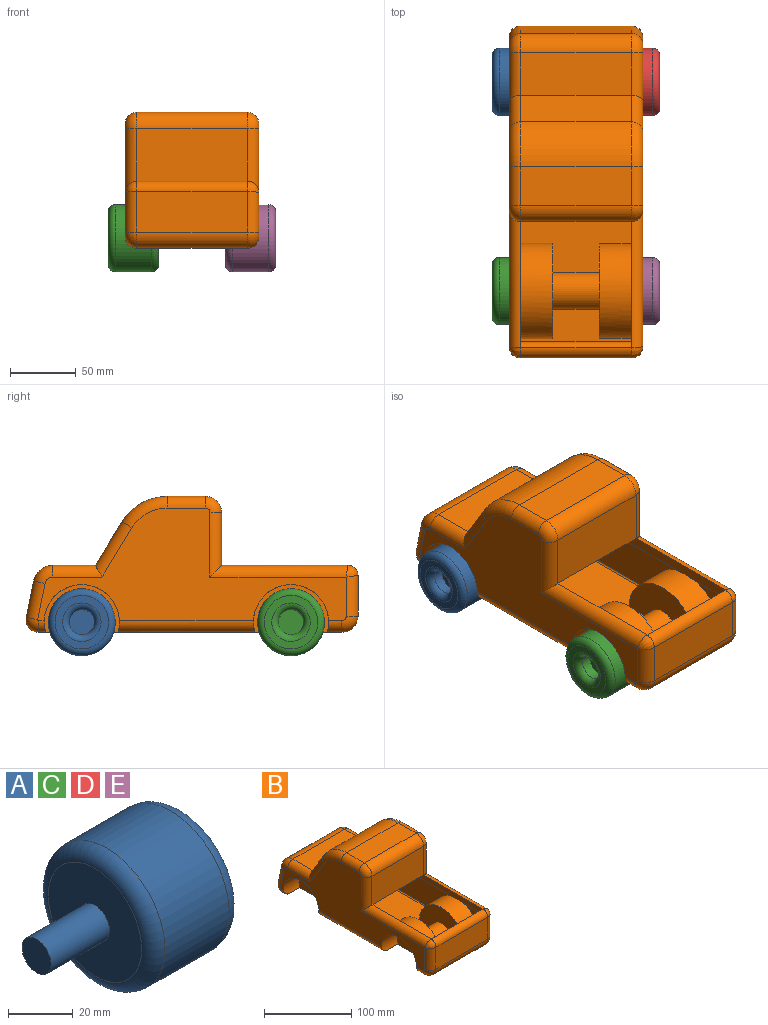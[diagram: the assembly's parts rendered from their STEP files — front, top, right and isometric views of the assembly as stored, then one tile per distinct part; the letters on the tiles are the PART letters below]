
ASSEMBLY  parts=5 mates=4
PART A: 10 faces, bbox 63.5x55x55 mm
  f0: cylinder r=6.35mm len=25.4mm, axis (-1,0,0), area 1013.4mm2, adj f1,f4
  f1: plane 12.7x12.7mm, normal (-1,0,0), area 126.7mm2, adj f0
  f2: cylinder r=25.4mm len=50.8mm, axis (-1,0,0), area 4459mm2, adj f8,f9
  f3: plane 40.64x40.64mm, normal (1,0,0), area 627.1mm2, adj f7,f9
  f4: plane 40.64x40.64mm, normal (-1,0,0), area 1170.5mm2, adj f0,f8
  f5: cylinder r=9.53mm len=19.05mm, axis (1,0,0), area 456mm2, adj f6,f7
  f6: plane 19.05x19.05mm, normal (1,0,0), area 285mm2, adj f5
  f7: torus R=14.61mm, axis (1,0,0), area 570.1mm2, adj f3,f5
  f8: torus R=20.32mm, axis (1,0,0), area 1180.9mm2, adj f2,f4
  f9: torus R=20.32mm, axis (1,0,0), area 1180.9mm2, adj f2,f3
PART B: 126 faces, bbox 101.6x251.9x106.5 mm
  f0: plane 234.13x85.37mm, normal (-1,0,0), area 8596.9mm2, adj f20,f22,f25,f26,f27,f29,f30,f31
  f1: cylinder r=40.13mm len=83.82mm, axis (-1,0,0), area 3441.9mm2, adj f2,f13,f33,f48
  f2: plane 83.82x29.03mm, normal (0,0,1), area 2433.6mm2, adj f1,f3,f32,f47
  f3: cylinder r=12.28mm len=83.82mm, axis (-1,0,0), area 1617.1mm2, adj f2,f4,f31,f46
  f4: plane 83.82x40.06mm, normal (0,-1,0), area 3358.1mm2, adj f3,f30,f45,f83
  f5: cylinder r=7.7mm len=83.82mm, axis (-1,0,0), area 1014.3mm2, adj f6,f28,f43,f76
  f6: plane 83.82x30.81mm, normal (0,-1,0), area 2582.8mm2, adj f5,f7,f27,f42
  f7: cylinder r=12.28mm len=83.82mm, axis (-1,0,0), area 1617.1mm2, adj f6,f8,f26,f41
  f8: plane 230.21x83.82mm, normal (0,0,-1), area 15669.6mm2, adj f7,f9,f15,f16,f17,f18,f19,f20
  f9: cylinder r=9.41mm len=83.82mm, axis (-1,0,0), area 1396.9mm2, adj f8,f10,f38,f53
  f10: plane 83.82x27.51mm, normal (0,0.98,0.2), area 2352.1mm2, adj f9,f11,f37,f52
  f11: cylinder r=14.98mm len=83.82mm, axis (-1,0,0), area 1722.4mm2, adj f10,f12,f36,f51
  f12: plane 83.82x32.24mm, normal (0,0,1), area 2702.5mm2, adj f11,f13,f35,f50
  f13: plane 83.82x33.11mm, normal (0,0.85,0.52), area 3250.5mm2, adj f1,f12,f34,f49
  f14: plane 234.13x85.37mm, normal (1,0,0), area 8624.5mm2, adj f16,f18,f40,f41,f42,f44,f45,f46
  f15: plane 57.15x36.2mm, normal (1,0,0), area 1586.2mm2, adj f8,f16,f23
  f16: cylinder r=28.57mm len=57.15mm, axis (1,0,0), area 2637.4mm2, adj f8,f14,f15,f54,f56
  f17: plane 56.52x35.88mm, normal (1,0,0), area 1552.9mm2, adj f8,f18,f24
  f18: cylinder r=28.26mm len=56.52mm, axis (1,0,0), area 2612.1mm2, adj f8,f14,f17,f40,f56
  f19: plane 57.15x36.2mm, normal (-1,0,0), area 1586.2mm2, adj f8,f20,f23
  f20: cylinder r=28.57mm len=57.15mm, axis (-1,0,0), area 2637.4mm2, adj f0,f8,f19,f39,f55
  f21: plane 57.15x36.2mm, normal (-1,0,0), area 1586.2mm2, adj f8,f22,f24
  f22: cylinder r=28.57mm len=57.15mm, axis (-1,0,0), area 2637.4mm2, adj f0,f8,f21,f25,f55
  f23: cylinder r=6.35mm len=50.8mm, axis (-1,0,0), area 2026.8mm2, adj f15,f19
  f24: cylinder r=6.35mm len=50.8mm, axis (-1,0,0), area 2026.8mm2, adj f17,f21
  f25: cylinder r=8.89mm len=10.98mm, axis (0,1,0), area 145.5mm2, adj f0,f8,f22,f26
  f26: torus R=3.39mm, axis (1,0,0), area 198.6mm2, adj f0,f7,f25,f27
  f27: cylinder r=8.89mm len=30.81mm, axis (0,0,-1), area 424.3mm2, adj f0,f6,f26,f28
  f28: bspline ~11.03x8.89mm, area 109mm2, adj f5,f27,f29
  f29: cylinder r=8.89mm len=104.65mm, axis (0,-1,0), area 1376.3mm2, adj f0,f28,f30,f77
  f30: cylinder r=8.89mm len=48.95mm, axis (0,0,-1), area 604.6mm2, adj f0,f4,f29,f31
  f31: torus R=3.39mm, axis (1,0,0), area 198.6mm2, adj f0,f3,f30,f32
  f32: cylinder r=8.89mm len=29.03mm, axis (0,-1,0), area 405.4mm2, adj f0,f2,f31,f33
  f33: torus R=31.24mm, axis (1,0,0), area 527.3mm2, adj f0,f1,f32,f34
  f34: cylinder r=8.89mm len=42mm, axis (0,-0.52,0.85), area 566.9mm2, adj f0,f13,f33,f35
  f35: cylinder r=8.89mm len=37.23mm, axis (0,-1,0), area 475.6mm2, adj f0,f12,f34,f36
  f36: torus R=6.09mm, axis (1,0,0), area 225.1mm2, adj f0,f11,f35,f37
  f37: cylinder r=8.89mm len=29.27mm, axis (0,-0.2,0.98), area 391.9mm2, adj f0,f10,f36,f38
  f38: torus R=0.52mm, axis (1,0,0), area 152.9mm2, adj f0,f9,f37,f39
  f39: cylinder r=8.89mm len=8.89mm, axis (0,1,0), area 67.6mm2, adj f0,f8,f20,f38
  f40: cylinder r=8.89mm len=11.31mm, axis (0,-1,0), area 150mm2, adj f8,f14,f18,f41
  f41: torus R=3.39mm, axis (1,0,0), area 198.6mm2, adj f7,f14,f40,f42
  f42: cylinder r=8.89mm len=30.81mm, axis (0,0,1), area 424.3mm2, adj f6,f14,f41,f43
  f43: bspline ~11.03x8.89mm, area 109mm2, adj f5,f42,f44
  f44: cylinder r=8.89mm len=104.65mm, axis (0,1,0), area 1376.3mm2, adj f14,f43,f45,f75
  f45: cylinder r=8.89mm len=48.95mm, axis (0,0,1), area 604.6mm2, adj f4,f14,f44,f46
  f46: torus R=3.39mm, axis (1,0,0), area 198.6mm2, adj f3,f14,f45,f47
  f47: cylinder r=8.89mm len=29.03mm, axis (0,1,0), area 405.4mm2, adj f2,f14,f46,f48
  f48: torus R=31.24mm, axis (1,0,0), area 527.3mm2, adj f1,f14,f47,f49
  f49: cylinder r=8.89mm len=42mm, axis (0,0.52,-0.85), area 566.9mm2, adj f13,f14,f48,f50
  f50: cylinder r=8.89mm len=37.23mm, axis (0,1,0), area 475.6mm2, adj f12,f14,f49,f51
  f51: torus R=6.09mm, axis (1,0,0), area 225.1mm2, adj f11,f14,f50,f52
  f52: cylinder r=8.89mm len=29.27mm, axis (0,0.2,-0.98), area 391.9mm2, adj f10,f14,f51,f53
  f53: torus R=0.52mm, axis (1,0,0), area 152.9mm2, adj f9,f14,f52,f54
  f54: cylinder r=8.89mm len=8.89mm, axis (0,-1,0), area 67.6mm2, adj f8,f14,f16,f53
  f55: cylinder r=8.89mm len=103.67mm, axis (0,1,0), area 1432mm2, adj f0,f8,f20,f22
  f56: cylinder r=8.89mm len=104mm, axis (0,-1,0), area 1436.5mm2, adj f8,f14,f16,f18
  f57: cylinder r=36.2mm len=72.39mm, axis (-1,0,0), area 2867.1mm2, adj f65,f66,f67,f73,f77,f78,f95,f98
  f58: plane 70.93x35.56mm, normal (1,0,0), area 1720.6mm2, adj f59,f61,f65,f87,f88,f90,f94,f96
  f59: cylinder r=36.2mm len=25.4mm, axis (-1,0,0), area 798.2mm2, adj f58,f61,f74,f90,f108,f110
  f60: plane 70.93x35.56mm, normal (-1,0,0), area 1720.6mm2, adj f61,f62,f63,f65,f87,f88,f90,f96
  f61: plane 83.82x27.51mm, normal (0,-0.98,-0.2), area 1584.6mm2, adj f58,f59,f60,f63,f88,f89,f110,f123
  f62: cylinder r=36.2mm len=35.56mm, axis (1,0,0), area 1269.7mm2, adj f60,f65,f69,f72,f90,f125
  f63: cylinder r=36.2mm len=25.4mm, axis (1,0,0), area 798.2mm2, adj f60,f61,f71,f90,f121,f123
  f64: cylinder r=35.88mm len=71.76mm, axis (1,0,0), area 2846.1mm2, adj f65,f66,f70,f72,f75,f92,f93,f111
  f65: plane 130.81x83.82mm, normal (0,0,1), area 8827mm2, adj f57,f58,f60,f62,f64,f93,f94,f95
  f66: plane 83.82x24.55mm, normal (0,0,1), area 992.7mm2, adj f57,f64,f86,f93,f95,f97,f98,f111
  f67: cylinder r=1.27mm len=36.35mm, axis (0,-1,0), area 67.8mm2, adj f57,f77,f78,f101
  f68: cylinder r=1.27mm len=8.56mm, axis (0,-1,0), area 12.3mm2, adj f73,f90,f94,f107
  f69: cylinder r=1.27mm len=8.56mm, axis (0,1,0), area 12.3mm2, adj f62,f72,f90,f120
  f70: cylinder r=1.27mm len=38.33mm, axis (0,1,0), area 70.8mm2, adj f64,f75,f92,f114
  f71: plane 18.05x13.52mm, normal (-1,0,0), area 71.4mm2, adj f63,f121,f122,f123
  f72: plane 136.61x85.37mm, normal (-1,0,0), area 6719.5mm2, adj f62,f64,f69,f115,f116,f117,f118,f119
  f73: plane 135.57x85.37mm, normal (1,0,0), area 6705.6mm2, adj f57,f68,f94,f102,f103,f104,f105,f106
  f74: plane 18.05x13.52mm, normal (1,0,0), area 71.4mm2, adj f59,f108,f109,f110
  f75: plane 103.38x7.62mm, normal (-1,0,0), area 785.7mm2, adj f44,f64,f70,f76,f83,f115,f116
  f76: plane 83.82x7.62mm, normal (0,1,0), area 638.7mm2, adj f5,f75,f77,f84
  f77: plane 103.38x7.62mm, normal (1,0,0), area 782mm2, adj f29,f57,f67,f76,f83,f102,f103
  f78: plane 33.02x30.32mm, normal (1,0,0), area 413.2mm2, adj f57,f67,f98,f99,f100
  f79: cylinder r=32.51mm len=83.82mm, axis (-1,0,0), area 2788.4mm2, adj f80,f91,f106,f119
  f80: plane 83.82x29.03mm, normal (0,0,-1), area 2433.6mm2, adj f79,f81,f105,f118
  f81: cylinder r=4.66mm len=83.82mm, axis (-1,0,0), area 613.9mm2, adj f80,f82,f104,f117
  f82: plane 83.82x40.06mm, normal (0,1,0), area 3358.1mm2, adj f81,f83,f103,f116
  f83: plane 83.82x7.62mm, normal (0,0,-1), area 638.7mm2, adj f4,f75,f77,f82
  f84: cylinder r=0.08mm len=83.82mm, axis (-1,0,0), area 11.1mm2, adj f76,f85,f101,f114
  f85: plane 83.82x30.81mm, normal (0,1,0), area 2582.8mm2, adj f84,f86,f100,f113
  f86: cylinder r=4.66mm len=83.82mm, axis (-1,0,0), area 613.9mm2, adj f66,f85,f99,f112
  f87: plane 35.56x18.97mm, normal (0,0,1), area 674.7mm2, adj f58,f60,f88,f96
  f88: cylinder r=1.79mm len=35.56mm, axis (-1,0,0), area 112.9mm2, adj f58,f60,f61,f87
  f89: cylinder r=7.36mm len=83.82mm, axis (-1,0,0), area 846.5mm2, adj f61,f90,f109,f122
  f90: plane 83.82x36.52mm, normal (0,0,-1), area 2409.6mm2, adj f58,f59,f60,f62,f63,f68,f69,f89
  f91: plane 83.82x36.76mm, normal (0,-0.85,-0.52), area 3609.1mm2, adj f79,f90,f107,f120
  f92: plane 33.02x31.36mm, normal (-1,0,0), area 427.2mm2, adj f64,f70,f111,f112,f113
  f93: plane 71.76x35.88mm, normal (-1,0,0), area 1715.4mm2, adj f64,f65,f66,f97
  f94: cylinder r=36.2mm len=35.56mm, axis (-1,0,0), area 1269.7mm2, adj f58,f65,f68,f73,f90,f124
  f95: plane 72.39x36.2mm, normal (1,0,0), area 1751.3mm2, adj f57,f65,f66,f97
  f96: cylinder r=13.97mm len=35.56mm, axis (-1,0,0), area 1560.7mm2, adj f58,f60,f65,f87
  f97: cylinder r=13.97mm len=35.56mm, axis (-1,0,0), area 1560.7mm2, adj f65,f66,f93,f95
  f98: cylinder r=1.27mm len=2.35mm, axis (0,1,0), area 4.7mm2, adj f57,f66,f78,f99
  f99: torus R=3.39mm, axis (1,0,0), area 13.2mm2, adj f78,f86,f98,f100
  f100: cylinder r=1.27mm len=30.81mm, axis (0,0,-1), area 60.6mm2, adj f78,f85,f99,f101
  f101: bspline ~1.45x1.27mm, area 0.1mm2, adj f67,f84,f100
  f102: cylinder r=1.27mm len=54.8mm, axis (0,-1,0), area 103.8mm2, adj f57,f73,f77,f103
  f103: cylinder r=1.27mm len=48.95mm, axis (0,0,-1), area 96mm2, adj f73,f77,f82,f102,f104
  f104: torus R=3.39mm, axis (1,0,0), area 13.2mm2, adj f73,f81,f103,f105
  f105: cylinder r=1.27mm len=29.03mm, axis (0,-1,0), area 57.9mm2, adj f73,f80,f104,f106
  f106: torus R=31.24mm, axis (1,0,0), area 65.4mm2, adj f73,f79,f105,f107
  f107: cylinder r=1.27mm len=38.03mm, axis (0,-0.52,0.85), area 86.4mm2, adj f68,f73,f91,f106
  f108: cylinder r=1.27mm len=15.17mm, axis (0,-1,0), area 26.4mm2, adj f59,f74,f90,f109
  f109: torus R=6.09mm, axis (1,0,0), area 18.9mm2, adj f74,f89,f108,f110
  f110: cylinder r=1.27mm len=12.17mm, axis (0,-0.2,0.98), area 21.7mm2, adj f59,f61,f74,f109
  f111: cylinder r=1.27mm len=2.66mm, axis (0,-1,0), area 5.3mm2, adj f64,f66,f92,f112
  f112: torus R=3.39mm, axis (1,0,0), area 13.2mm2, adj f86,f92,f111,f113
  f113: cylinder r=1.27mm len=30.81mm, axis (0,0,1), area 60.6mm2, adj f85,f92,f112,f114
  f114: bspline ~1.45x1.27mm, area 0.1mm2, adj f70,f84,f113
  f115: cylinder r=1.27mm len=56.79mm, axis (0,1,0), area 106.8mm2, adj f64,f72,f75,f116
  f116: cylinder r=1.27mm len=48.95mm, axis (0,0,1), area 96mm2, adj f72,f75,f82,f115,f117
  f117: torus R=3.39mm, axis (1,0,0), area 13.2mm2, adj f72,f81,f116,f118
  f118: cylinder r=1.27mm len=29.03mm, axis (0,1,0), area 57.9mm2, adj f72,f80,f117,f119
  f119: torus R=31.24mm, axis (1,0,0), area 65.4mm2, adj f72,f79,f118,f120
  f120: cylinder r=1.27mm len=38.03mm, axis (0,0.52,-0.85), area 86.4mm2, adj f69,f72,f91,f119
  f121: cylinder r=1.27mm len=15.17mm, axis (0,1,0), area 26.4mm2, adj f63,f71,f90,f122
  f122: torus R=6.09mm, axis (1,0,0), area 18.9mm2, adj f71,f89,f121,f123
  f123: cylinder r=1.27mm len=12.17mm, axis (0,0.2,-0.98), area 21.7mm2, adj f61,f63,f71,f122
  f124: cylinder r=1.27mm len=86.4mm, axis (0,1,0), area 172.3mm2, adj f57,f65,f73,f94
  f125: cylinder r=1.27mm len=86.72mm, axis (0,-1,0), area 173mm2, adj f62,f64,f65,f72
PART C: same geometry as A
PART D: same geometry as A
PART E: same geometry as A
PLACE A rot(axis=(0,1,0),180deg) t=(13.3,161.23,60.97)mm
PLACE B t=(-37.5,-48.32,53.35)mm
PLACE C rot(axis=(0,-0.71,0.71),180deg) t=(13.3,2.48,60.97)mm
PLACE D t=(13.3,161.23,60.97)mm
PLACE E t=(13.3,2.48,60.97)mm
MATE planar C.f0 <-> B.f18  axis (1,0,0) through (-12.1,2.48,60.97)mm
MATE planar E.f0 <-> B.f18  axis (-1,0,0) through (13.3,2.48,60.97)mm
MATE planar E.f0 <-> B.f18  axis (-1,0,0) through (38.7,2.48,60.97)mm
MATE planar A.f0 <-> B.f16  axis (1,0,0) through (-12.1,161.23,60.97)mm
